# Revit family: Broan®-SKY_Series-Energy_Recovery_Ventilator-102_CFM_at_0.4_in._w.g
name_source: partatom
category: Mechanical Equipment
units: mm (PartAtom-declared; Revit-internal decimal feet)

## family parameters
Always vertical = No
Classification = None
Cut with Voids When Loaded = No
Part Type = Normal
Room Calculation Point = No
Round Connector Dimension = Use Diameter
Shared = No
Work Plane-Based = Yes

## types (1)
- ERV100S
    Air Volume = 100 CFM
    Default Elevation = 0.00"
    Exhaust Air Connection Diameter = 5"
    Fan Wattage = 96 W
    Frequency = 60 Hz
    Height = 9.00"
    Length = 20.00"
    Manufacturer = Broan
    Model = ERV100S
    Noise = 67.8
    Number of Poles = 1
    Operating Weight = 32.00 lb
    Phase = 1
    Power Factor = 0
    Product Documentation Link = https://www.broan-nutone.com
    Product Name = Broan® SKY Series Energy Recovery Ventilator, 102 CFM at 0.4 in. w.g.
    Product Page URL = https://www.broan-nutone.com
    Requirements and Standards = CSA C439
UL 1812
CSA C22.2
CSA C444
    Return Air Connection Diameter = 5"
    Supply Air Connection Diameter = 5"
    URL = https://www.broan-nutone.com
    Voltage = 120 V
    Width = 27.13"
    c Back Clearance = 0.00"
    c Front Clearance = 8.00"
    c Gen Diameter = 5.00"
    c Left Clearance = 8.00"
    c Lenght = 16.88"
    c MC width = 3.13"
    c Offset vent side = 4.75"
    c Right Clrearance = 8.00"
    c Top Clearance = 0.00"
    c Vent Height = 2.57"
    c Width = 22.00"

## geometry (parser evidence)
native form markers: Sweep x4
no freeform markers — native parametric forms only
